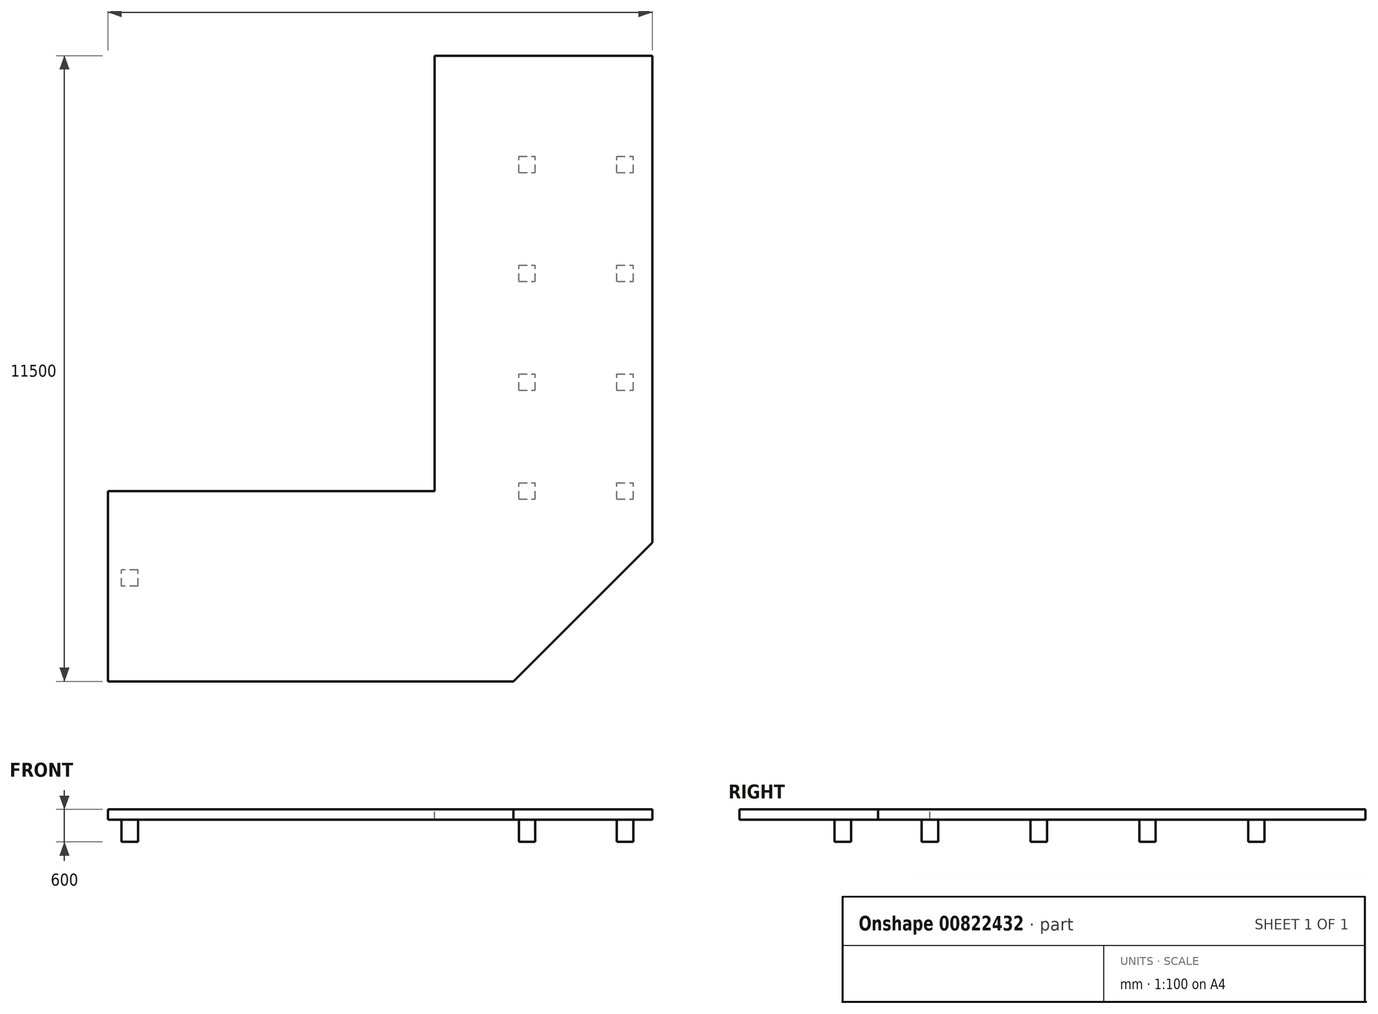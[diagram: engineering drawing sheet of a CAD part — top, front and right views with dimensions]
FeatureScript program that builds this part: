
annotation { "Feature Type Name" : "Feature", "Feature Type Description" : "" }
export const myFeature = defineFeature(function(context is Context, id is Id, definition is map)
    precondition{}
    {
        {
            var Q0;
            Q0=qCreatedBy(makeId("Top.planeOp"),FACE);
            var sketch = newSketch(context, id + "F0", { "sketchPlane" : qUnion([Q0])});
            skLineSegment(sketch, "E0", {"start": v(0, 8000) * mm, "end": v(0, 0) * mm});
            skLineSegment(sketch, "E1", {"start": v(0, 0) * mm, "end": v(0, 8000) * mm});
            skLineSegment(sketch, "E2", {"start": v(4000, 8000) * mm, "end": v(0, 8000) * mm});
            skLineSegment(sketch, "E3", {"start": v(4000, 8000) * mm, "end": v(4000, -949.75) * mm});
            skLineSegment(sketch, "E4", {"start": v(4000, -949.75) * mm, "end": v(1449.75, -3500) * mm});
            skLineSegment(sketch, "E5", {"start": v(1449.75, -3500) * mm, "end": v(-6000, -3500) * mm});
            skLineSegment(sketch, "E6", {"start": v(-6000, -3500) * mm, "end": v(-6000, 0) * mm});
            skLineSegment(sketch, "E7", {"start": v(-6000, 0) * mm, "end": v(0, 0) * mm});
            skSolve(sketch);
        }
        {
            var Q0;
            Q0 = qSketchRegion(id + "F0", true);
            extrude(context, id + "F1", {"entities" : qUnion([Q0]), "oppositeDirection" : true, "depth" : 193 * mm, "offsetDistance" : 25 * mm});
        }
        {
            var Q0;
            Q0=qCreatedBy(makeId("Top.planeOp"),FACE);
            var sketch = newSketch(context, id + "F2", { "sketchPlane" : qUnion([Q0])});
            skLineSegment(sketch, "E8.bottom", {"start": v(1550, 5850) * mm, "end": v(1850, 5850) * mm});
            skLineSegment(sketch, "E8.top", {"start": v(1550, 6150) * mm, "end": v(1850, 6150) * mm});
            skLineSegment(sketch, "E8.left", {"start": v(1550, 5850) * mm, "end": v(1550, 6150) * mm});
            skLineSegment(sketch, "E8.right", {"start": v(1850, 5850) * mm, "end": v(1850, 6150) * mm});
            skPoint(sketch, "E8.middle", {"position": v(1700, 6000) * mm});
            skLineSegment(sketch, "E9.0.1.0", {"start": v(1550, 3850) * mm, "end": v(1850, 3850) * mm});
            skLineSegment(sketch, "E9.0.1.1", {"start": v(1550, 3850) * mm, "end": v(1550, 4150) * mm});
            skLineSegment(sketch, "E9.0.1.2", {"start": v(1850, 3850) * mm, "end": v(1850, 4150) * mm});
            skLineSegment(sketch, "E9.0.1.3", {"start": v(1550, 4150) * mm, "end": v(1850, 4150) * mm});
            skLineSegment(sketch, "E9.0.2.0", {"start": v(1550, 1850) * mm, "end": v(1850, 1850) * mm});
            skLineSegment(sketch, "E9.0.2.1", {"start": v(1550, 1850) * mm, "end": v(1550, 2150) * mm});
            skLineSegment(sketch, "E9.0.2.2", {"start": v(1850, 1850) * mm, "end": v(1850, 2150) * mm});
            skLineSegment(sketch, "E9.0.2.3", {"start": v(1550, 2150) * mm, "end": v(1850, 2150) * mm});
            skLineSegment(sketch, "E9.0.3.0", {"start": v(1550, -150) * mm, "end": v(1850, -150) * mm});
            skLineSegment(sketch, "E9.0.3.1", {"start": v(1550, -150) * mm, "end": v(1550, 150) * mm});
            skLineSegment(sketch, "E9.0.3.2", {"start": v(1850, -150) * mm, "end": v(1850, 150) * mm});
            skLineSegment(sketch, "E9.0.3.3", {"start": v(1550, 150) * mm, "end": v(1850, 150) * mm});
            skLineSegment(sketch, "E9.1.0.0", {"start": v(3350, 5850) * mm, "end": v(3650, 5850) * mm});
            skLineSegment(sketch, "E9.1.0.1", {"start": v(3350, 5850) * mm, "end": v(3350, 6150) * mm});
            skLineSegment(sketch, "E9.1.0.2", {"start": v(3650, 5850) * mm, "end": v(3650, 6150) * mm});
            skLineSegment(sketch, "E9.1.0.3", {"start": v(3350, 6150) * mm, "end": v(3650, 6150) * mm});
            skLineSegment(sketch, "E9.1.1.0", {"start": v(3350, 3850) * mm, "end": v(3650, 3850) * mm});
            skLineSegment(sketch, "E9.1.1.1", {"start": v(3350, 3850) * mm, "end": v(3350, 4150) * mm});
            skLineSegment(sketch, "E9.1.1.2", {"start": v(3650, 3850) * mm, "end": v(3650, 4150) * mm});
            skLineSegment(sketch, "E9.1.1.3", {"start": v(3350, 4150) * mm, "end": v(3650, 4150) * mm});
            skLineSegment(sketch, "E9.1.2.0", {"start": v(3350, 1850) * mm, "end": v(3650, 1850) * mm});
            skLineSegment(sketch, "E9.1.2.1", {"start": v(3350, 1850) * mm, "end": v(3350, 2150) * mm});
            skLineSegment(sketch, "E9.1.2.2", {"start": v(3650, 1850) * mm, "end": v(3650, 2150) * mm});
            skLineSegment(sketch, "E9.1.2.3", {"start": v(3350, 2150) * mm, "end": v(3650, 2150) * mm});
            skLineSegment(sketch, "E9.1.3.0", {"start": v(3350, -150) * mm, "end": v(3650, -150) * mm});
            skLineSegment(sketch, "E9.1.3.1", {"start": v(3350, -150) * mm, "end": v(3350, 150) * mm});
            skLineSegment(sketch, "E9.1.3.2", {"start": v(3650, -150) * mm, "end": v(3650, 150) * mm});
            skLineSegment(sketch, "E9.1.3.3", {"start": v(3350, 150) * mm, "end": v(3650, 150) * mm});
            skLineSegment(sketch, "E9.direction1", {"start": v(1550, 5850) * mm, "end": v(3350, 5850) * mm, "construction": true});
            skLineSegment(sketch, "E9.direction2", {"start": v(1550, 5850) * mm, "end": v(1550, 3850) * mm, "construction": true});
            skLineSegment(sketch, "E10.bottom", {"start": v(-5450, -1750) * mm, "end": v(-5750, -1750) * mm});
            skLineSegment(sketch, "E10.top", {"start": v(-5450, -1450) * mm, "end": v(-5750, -1450) * mm});
            skLineSegment(sketch, "E10.left", {"start": v(-5450, -1750) * mm, "end": v(-5450, -1450) * mm});
            skLineSegment(sketch, "E10.right", {"start": v(-5750, -1750) * mm, "end": v(-5750, -1450) * mm});
            skPoint(sketch, "E10.middle", {"position": v(-5600, -1600) * mm});
            skSolve(sketch);
        }
        {
            var Q0;
            Q0 = qSketchRegion(id + "F2", true);
            extrude(context, id + "F3", {"entities" : qUnion([Q0]), "operationType" : NewBodyOperationType.ADD, "oppositeDirection" : true, "depth" : 600 * mm, "offsetDistance" : 25 * mm});
        }
    });
